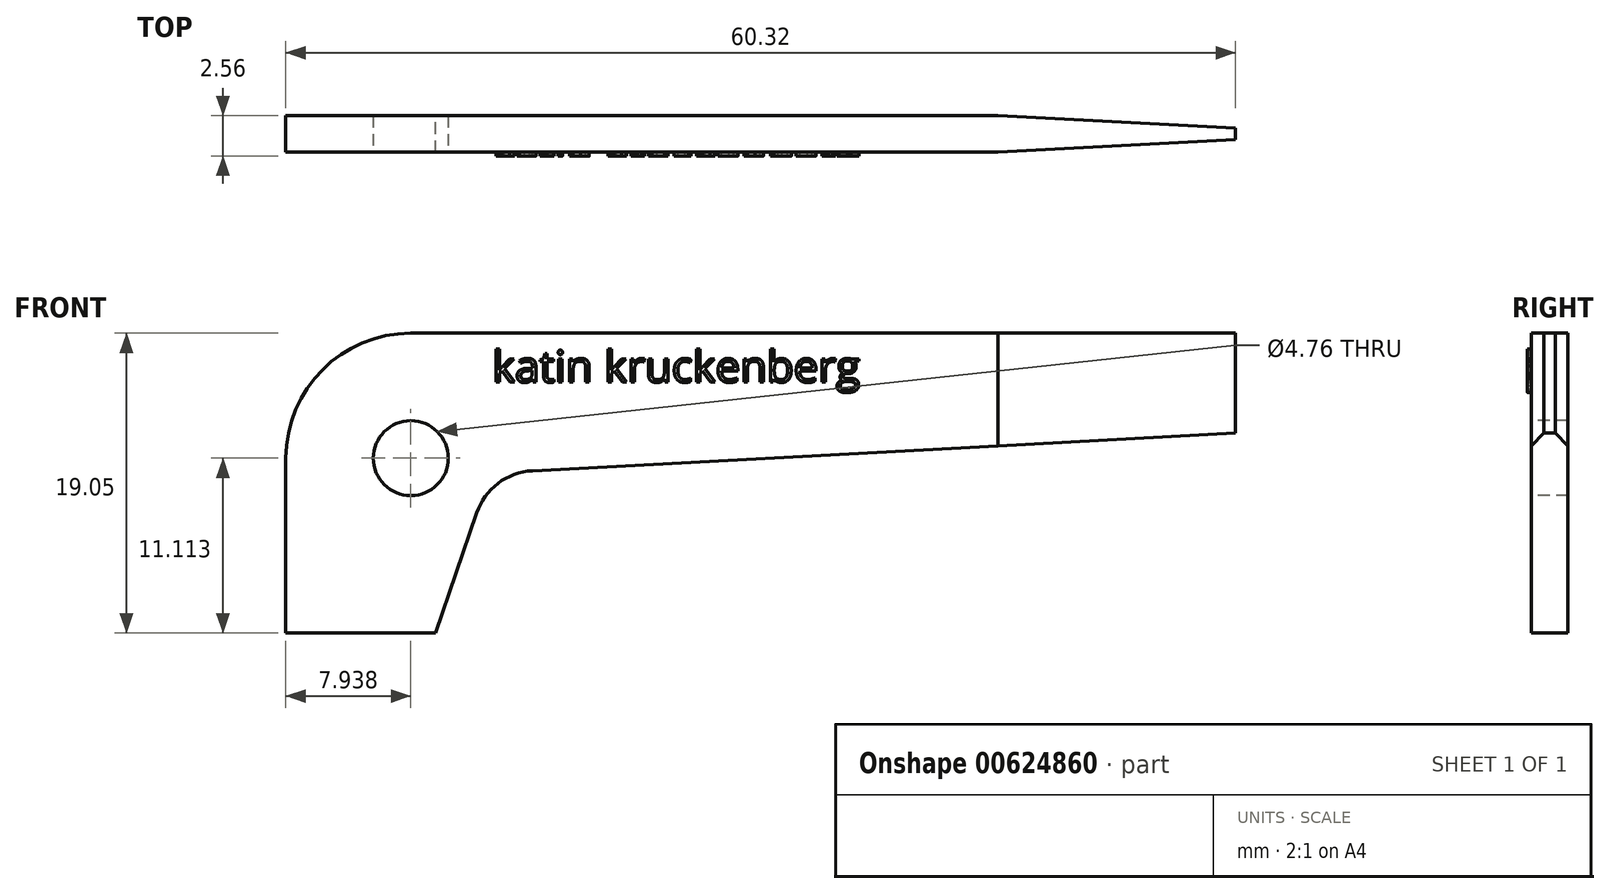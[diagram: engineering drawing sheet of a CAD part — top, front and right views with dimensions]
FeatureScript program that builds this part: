
annotation { "Feature Type Name" : "Feature", "Feature Type Description" : "" }
export const myFeature = defineFeature(function(context is Context, id is Id, definition is map)
    precondition{}
    {
        {
            var Q0;
            Q0=qCreatedBy(makeId("Front.planeOp"),FACE);
            var sketch = newSketch(context, id + "F0", { "sketchPlane" : qUnion([Q0])});
            skLineSegment(sketch, "E0.top", {"start": v(7.94, 19.05) * mm, "end": v(60.33, 19.05) * mm});
            skLineSegment(sketch, "E0.left", {"start": v(0, 0) * mm, "end": v(0, 11.11) * mm});
            skLineSegment(sketch, "E1", {"start": v(9.53, 0) * mm, "end": v(12.12, 7.63) * mm});
            skLineSegment(sketch, "E2", {"start": v(60.33, 12.7) * mm, "end": v(15.66, 10.31) * mm});
            skLineSegment(sketch, "E3", {"start": v(9.53, 0) * mm, "end": v(0, 0) * mm});
            skLineSegment(sketch, "E4", {"start": v(60.33, 19.05) * mm, "end": v(60.33, 12.7) * mm});
            skArc(sketch, "E5", {"start": v(15.66, 10.31) * mm, "mid": v(13.48, 9.51) * mm, "end": v(12.12, 7.63) * mm});
            skPoint(sketch, "E6.visualSharp", {"position": v(0, 19.05) * mm});
            skArc(sketch, "E6.filletArc", {"start": v(7.94, 19.05) * mm, "mid": v(2.32, 16.73) * mm, "end": v(0, 11.11) * mm});
            skSolve(sketch);
        }
        {
            var Q0;
            Q0 = qSketchRegion(id + "F0", true);
            extrude(context, id + "F1", {"entities" : qUnion([Q0]), "depth" : 2.3 * mm, "offsetDistance" : 25.4 * mm});
        }
        {
            var Q0;
            Q0=makeQuery(id+"F1.opExtrude","CAP_FACE",FACE,{"disambiguationData":[OSD([sQuery(id+"F0.wireOp",EDGE,"E0.top"),sQuery(id+"F0.wireOp",EDGE,"E0.left"),sQuery(id+"F0.wireOp",EDGE,"E1"),sQuery(id+"F0.wireOp",EDGE,"E2"),sQuery(id+"F0.wireOp",EDGE,"E3"),sQuery(id+"F0.wireOp",EDGE,"E4"),sQuery(id+"F0.wireOp",EDGE,"E5"),sQuery(id+"F0.wireOp",EDGE,"E6.filletArc")])],"isStart":false});
            var sketch = newSketch(context, id + "F2", { "sketchPlane" : qUnion([Q0])});
            skCircle(sketch, "E7", {"center": v(7.94, 11.11) * mm, "radius": 2.38 * mm});
            skSolve(sketch);
        }
        {
            var Q0;
            Q0=makeQuery(id+"F2.imprint","IMPRINT",FACE,{"disambiguationData":[TD([[makeQuery(id+"F2.imprint","IMPRINT",EDGE,{"derivedFrom":sQuery(id+"F2.wireOp",EDGE,"E7")}),1.0]])]});
            extrude(context, id + "F3", {"entities" : qUnion([Q0]), "operationType" : NewBodyOperationType.REMOVE, "endBound" : BoundingType.THROUGH_ALL, "oppositeDirection" : true, "depth" : 25.4 * mm, "offsetDistance" : 25.4 * mm});
        }
        {
            var Q0;
            Q0=makeQuery(id+"F1.opExtrude","SWEPT_FACE",FACE,{"disambiguationData":[OSD([sQuery(id+"F0.wireOp",EDGE,"E0.top")])]});
            var sketch = newSketch(context, id + "F4", { "sketchPlane" : qUnion([Q0])});
            skLineSegment(sketch, "E8", {"start": v(45.24, 0) * mm, "end": v(60.33, -0.8) * mm});
            skPoint(sketch, "E9.endSnap0", {"position": v(60.33, -1.15) * mm});
            skLineSegment(sketch, "E10.MirrorCS", {"start": v(45.24, -2.3) * mm, "end": v(60.33, -1.52) * mm});
            skSolve(sketch);
        }
        {
            var Q0;
            {var subQ0=sQuery(id+"F4.wireOp",EDGE,"E8");Q0=makeQuery(id+"F4.imprint","IMPRINT",FACE,{"disambiguationData":[TD([[makeQuery(id+"F4.imprint","IMPRINT",EDGE,{"derivedFrom":subQ0}),1.0]])]});}
            var Q1;
            {var subQ0=sQuery(id+"F4.wireOp",EDGE,"E10.MirrorCS");Q1=makeQuery(id+"F4.imprint","IMPRINT",FACE,{"disambiguationData":[TD([[makeQuery(id+"F4.imprint","IMPRINT",EDGE,{"derivedFrom":subQ0}),-1.0]])]});}
            extrude(context, id + "F5", {"entities" : qUnion([Q0, Q1]), "operationType" : NewBodyOperationType.REMOVE, "oppositeDirection" : true, "depth" : 25.4 * mm, "offsetDistance" : 25.4 * mm});
        }
        {
            var Q0;
            Q0=makeQuery(id+"F1.opExtrude","CAP_FACE",FACE,{"disambiguationData":[OSD([sQuery(id+"F0.wireOp",EDGE,"E0.top"),sQuery(id+"F0.wireOp",EDGE,"E0.left"),sQuery(id+"F0.wireOp",EDGE,"E1"),sQuery(id+"F0.wireOp",EDGE,"E2"),sQuery(id+"F0.wireOp",EDGE,"E3"),sQuery(id+"F0.wireOp",EDGE,"E4"),sQuery(id+"F0.wireOp",EDGE,"E5"),sQuery(id+"F0.wireOp",EDGE,"E6.filletArc")])],"isStart":false});
            var sketch = newSketch(context, id + "F6", { "sketchPlane" : qUnion([Q0])});
            skText(sketch, "E11", { "text": "katin kruckenberg", "fontName": "OpenSans-Regular.ttf"});
            const initialGuessF6  = {"E11": [0.0131, 0.01594, 1, 0, 0.002]};
            skSetInitialGuess(sketch, initialGuessF6);
            skSolve(sketch);
        }
        {
            var Q0;
            Q0 = qSketchRegion(id + "F6", true);
            extrude(context, id + "F7", {"entities" : qUnion([Q0]), "operationType" : NewBodyOperationType.ADD, "depth" : 0.25 * mm, "offsetDistance" : 25.4 * mm});
        }
    });
